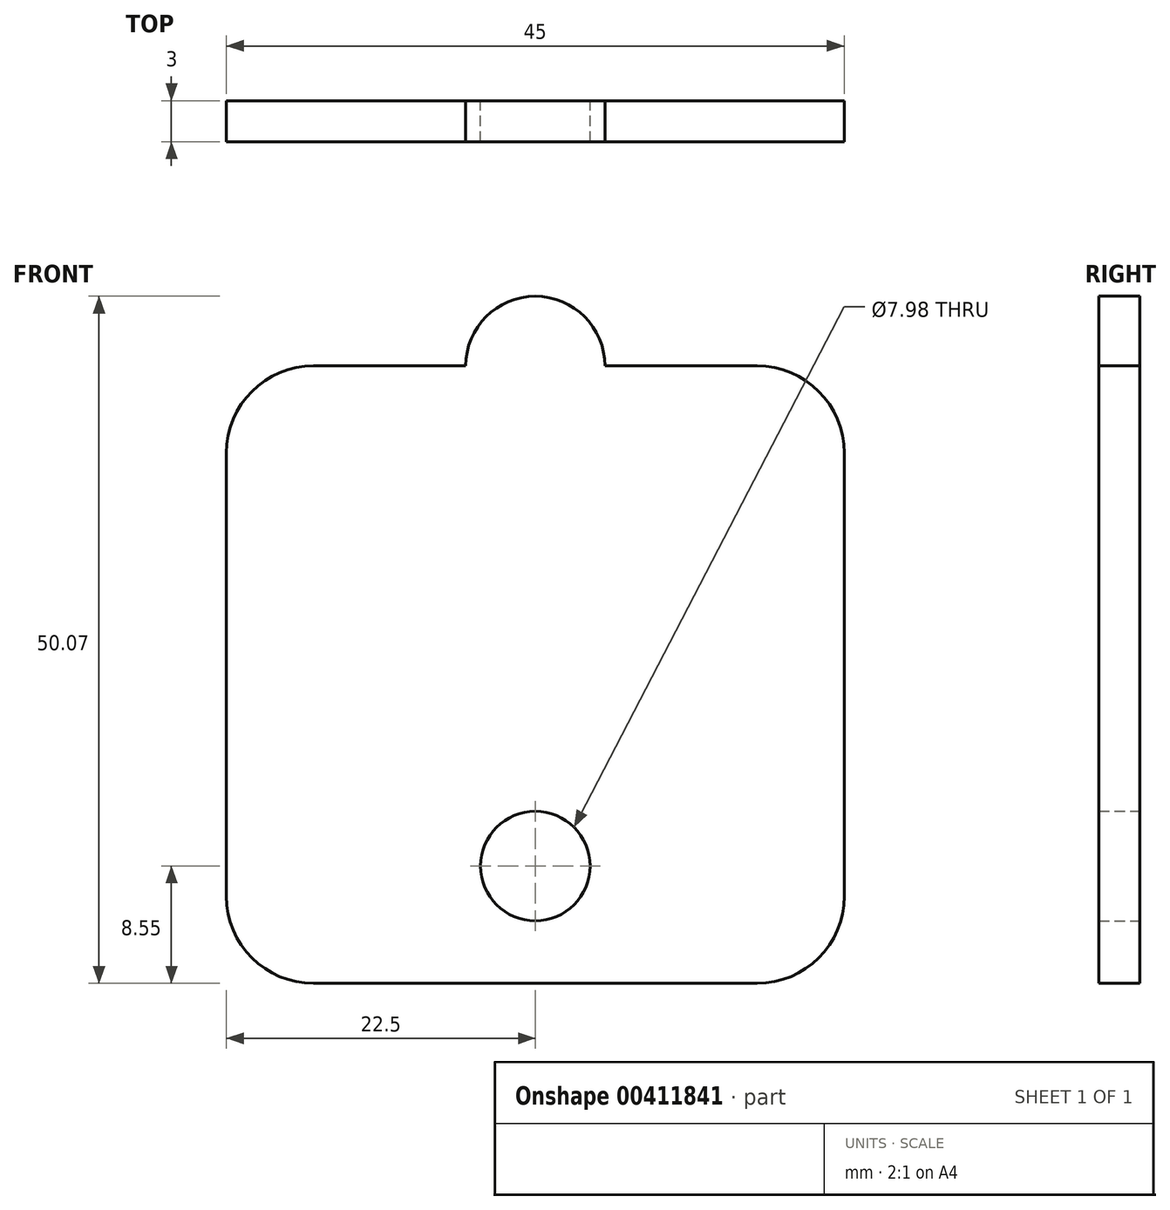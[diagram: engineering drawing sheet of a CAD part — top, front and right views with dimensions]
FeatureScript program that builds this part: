
annotation { "Feature Type Name" : "Feature", "Feature Type Description" : "" }
export const myFeature = defineFeature(function(context is Context, id is Id, definition is map)
    precondition{}
    {
        {
            var Q0;
            Q0=qCreatedBy(makeId("Front.planeOp"),FACE);
            var sketch = newSketch(context, id + "F0", { "sketchPlane" : qUnion([Q0])});
            skLineSegment(sketch, "E0.bottom", {"start": v(16.15, 22.5) * mm, "end": v(-16.15, 22.5) * mm});
            skLineSegment(sketch, "E0.top", {"start": v(16.15, -22.5) * mm, "end": v(-16.15, -22.5) * mm});
            skLineSegment(sketch, "E0.left", {"start": v(22.5, 16.15) * mm, "end": v(22.5, -16.15) * mm});
            skLineSegment(sketch, "E0.right", {"start": v(-22.5, 16.15) * mm, "end": v(-22.5, -16.15) * mm});
            skPoint(sketch, "E0.middle", {"position": v(0, 0) * mm});
            skCircle(sketch, "E1", {"center": v(0, 22.5) * mm, "radius": 5.07 * mm});
            skPoint(sketch, "E2.visualSharp", {"position": v(-22.5, 22.5) * mm});
            skArc(sketch, "E2.filletArc", {"start": v(-21.42, 22.5) * mm, "mid": v(-22.18, 22.18) * mm, "end": v(-22.5, 21.42) * mm});
            skArc(sketch, "E3.filletArc", {"start": v(-16.15, 22.5) * mm, "mid": v(-20.64, 20.64) * mm, "end": v(-22.5, 16.15) * mm});
            skPoint(sketch, "E4.visualSharp", {"position": v(22.5, 22.5) * mm});
            skArc(sketch, "E4.filletArc", {"start": v(22.5, 16.15) * mm, "mid": v(20.64, 20.64) * mm, "end": v(16.15, 22.5) * mm});
            skPoint(sketch, "E5.visualSharp", {"position": v(-22.5, -22.5) * mm});
            skArc(sketch, "E5.filletArc", {"start": v(-22.5, -16.15) * mm, "mid": v(-20.64, -20.64) * mm, "end": v(-16.15, -22.5) * mm});
            skPoint(sketch, "E6.visualSharp", {"position": v(22.5, -22.5) * mm});
            skArc(sketch, "E6.filletArc", {"start": v(16.15, -22.5) * mm, "mid": v(20.64, -20.64) * mm, "end": v(22.5, -16.15) * mm});
            skCircle(sketch, "E7", {"center": v(0, -13.95) * mm, "radius": 3.99 * mm});
            skSolve(sketch);
        }
        {
            var Q0;
            Q0=makeQuery(id+"F0.imprint","IMPRINT",FACE,{"disambiguationData":[TD([[makeQuery(id+"F0.imprint","IMPRINT",EDGE,{"derivedFrom":sQuery(id+"F0.wireOp",EDGE,"E0.top")}),-1.0]])]});
            var Q1;
            {var subQ0=sQuery(id+"F0.wireOp",EDGE,"E1");var subQ1=sQuery(id+"F0.wireOp",EDGE,"E0.bottom");var subQ2=makeQuery(id+"F0.imprint","INTERSECT",VERTEX,{"disambiguationData":[OD(0.0)],"derivedFrom":[subQ1,subQ0]});Q1=makeQuery(id+"F0.imprint","IMPRINT",FACE,{"disambiguationData":[TD([[makeQuery(id+"F0.imprint","IMPRINT",EDGE,{"disambiguationData":[TD([[subQ2,-1.0]])],"derivedFrom":subQ1}),-1.0]])]});}
            var Q2;
            {var subQ0=sQuery(id+"F0.wireOp",EDGE,"E1");var subQ1=sQuery(id+"F0.wireOp",EDGE,"E0.bottom");var subQ2=makeQuery(id+"F0.imprint","INTERSECT",VERTEX,{"disambiguationData":[OD(0.0)],"derivedFrom":[subQ1,subQ0]});Q2=makeQuery(id+"F0.imprint","IMPRINT",FACE,{"disambiguationData":[TD([[makeQuery(id+"F0.imprint","IMPRINT",EDGE,{"disambiguationData":[TD([[subQ2,-1.0]])],"derivedFrom":subQ1}),1.0]])]});}
            extrude(context, id + "F1", {"entities" : qUnion([Q0, Q1, Q2]), "depth" : 3 * mm});
        }
    });
